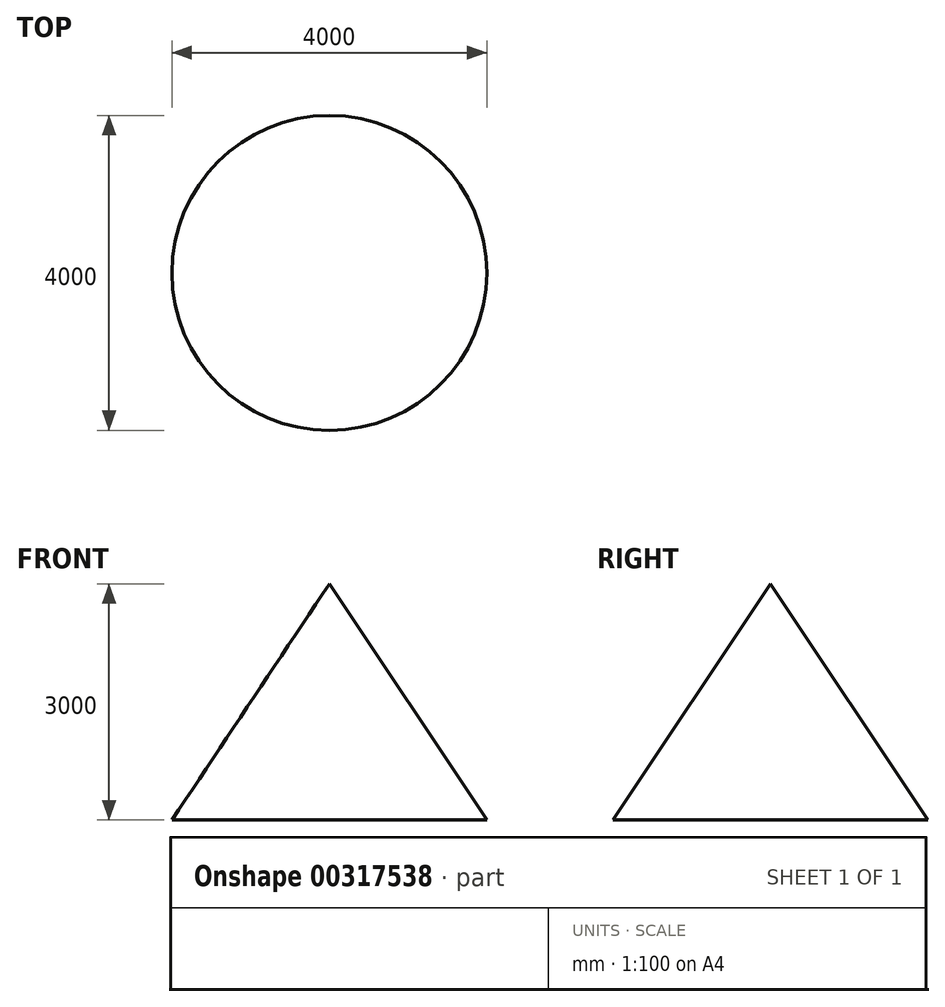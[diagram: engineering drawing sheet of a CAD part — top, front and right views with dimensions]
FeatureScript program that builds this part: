
annotation { "Feature Type Name" : "Feature", "Feature Type Description" : "" }
export const myFeature = defineFeature(function(context is Context, id is Id, definition is map)
    precondition{}
    {
        {
            var Q0;
            Q0=qCreatedBy(makeId("Front.planeOp"),FACE);
            var sketch = newSketch(context, id + "F0", { "sketchPlane" : qUnion([Q0])});
            skLineSegment(sketch, "E0", {"start": v(0, 0) * mm, "end": v(0, 3000) * mm});
            skLineSegment(sketch, "E1", {"start": v(0, 3000) * mm, "end": v(2000, 0) * mm});
            skLineSegment(sketch, "E2", {"start": v(2000, 0) * mm, "end": v(0, 0) * mm});
            skLineSegment(sketch, "E3", {"start": v(0, 3163.84) * mm, "end": v(0, 0) * mm, "construction": true});
            skSolve(sketch);
        }
        {
            var Q0;
            Q0=makeQuery(id+"F0.imprint","IMPRINT",FACE,{"disambiguationData":[TD([[makeQuery(id+"F0.imprint","IMPRINT",EDGE,{"derivedFrom":sQuery(id+"F0.wireOp",EDGE,"E0")}),-1.0]])]});
            var Q1;
            Q1=sQuery(id+"F0.wireOp",EDGE,"E3");
            revolve(context, id + "F1", {"entities" : qUnion([Q0]), "axis" : qUnion([Q1]), "revolveType" : RevolveType.FULL});
        }
    });
